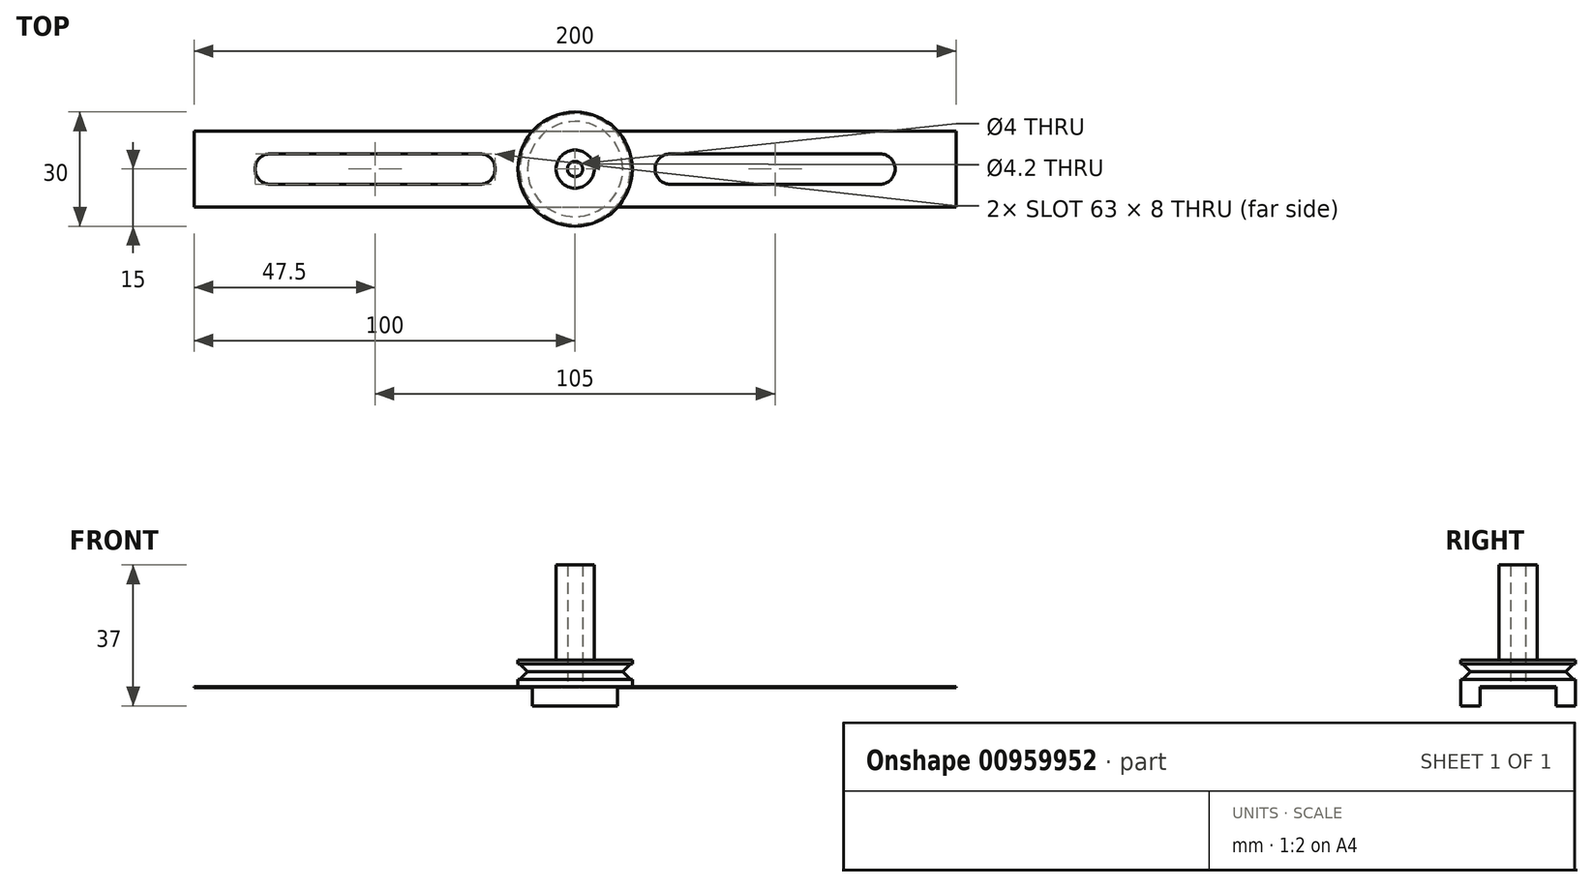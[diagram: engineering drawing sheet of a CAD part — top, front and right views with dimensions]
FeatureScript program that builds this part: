
annotation { "Feature Type Name" : "Feature", "Feature Type Description" : "" }
export const myFeature = defineFeature(function(context is Context, id is Id, definition is map)
    precondition{}
    {
        {
            var Q0;
            Q0=qCreatedBy(makeId("Top.planeOp"),FACE);
            var sketch = newSketch(context, id + "F0", { "sketchPlane" : qUnion([Q0])});
            skLineSegment(sketch, "E0.bottom", {"start": v(-100, 10) * mm, "end": v(100, 10) * mm});
            skLineSegment(sketch, "E0.top", {"start": v(-100, -10) * mm, "end": v(100, -10) * mm});
            skLineSegment(sketch, "E0.left", {"start": v(-100, 10) * mm, "end": v(-100, -10) * mm});
            skLineSegment(sketch, "E0.right", {"start": v(100, 10) * mm, "end": v(100, -10) * mm});
            skPoint(sketch, "E0.middle", {"position": v(0, 0) * mm});
            skSolve(sketch);
        }
        {
            var Q0;
            Q0 = qSketchRegion(id + "F0", true);
            extrude(context, id + "F1", {"entities" : qUnion([Q0]), "endBound" : BoundingType.SYMMETRIC, "oppositeDirection" : true, "depth" : 5 * mm, "offsetDistance" : 25 * mm});
        }
        {
            var Q0;
            Q0=qCreatedBy(makeId("Top.planeOp"),FACE);
            var sketch = newSketch(context, id + "F2", { "sketchPlane" : qUnion([Q0])});
            skCircle(sketch, "E1", {"center": v(0, 0) * mm, "radius": 2.1 * mm});
            skSolve(sketch);
        }
        {
            var Q0;
            Q0 = qSketchRegion(id + "F2", true);
            extrude(context, id + "F3", {"entities" : qUnion([Q0]), "operationType" : NewBodyOperationType.REMOVE, "endBound" : BoundingType.THROUGH_ALL, "depth" : 25 * mm, "offsetDistance" : 25 * mm, "hasSecondDirection" : true, "secondDirectionBound" : SecondDirectionBoundingType.THROUGH_ALL, "secondDirectionOppositeDirection" : true, "secondDirectionDepth" : 25 * mm});
        }
        {
            var Q0;
            Q0=qCreatedBy(makeId("Top.planeOp"),FACE);
            var sketch = newSketch(context, id + "F4", { "sketchPlane" : qUnion([Q0])});
            skLineSegment(sketch, "E2", {"start": v(0, 0) * mm, "end": v(0, 27.06) * mm, "construction": true});
            skLineSegment(sketch, "E3", {"start": v(-80, 0) * mm, "end": v(-25, 0) * mm});
            skArc(sketch, "E4.0.startCap", {"start": v(-80, -4) * mm, "mid": v(-84, 0) * mm, "end": v(-80, 4) * mm});
            skArc(sketch, "E4.0.endCap", {"start": v(-25, 4) * mm, "mid": v(-21, 0) * mm, "end": v(-25, -4) * mm});
            skLineSegment(sketch, "E4.0.left", {"start": v(-80, 4) * mm, "end": v(-25, 4) * mm});
            skLineSegment(sketch, "E4.0.right", {"start": v(-80, -4) * mm, "end": v(-25, -4) * mm});
            skArc(sketch, "E5.MirrorCS", {"start": v(25, 4) * mm, "mid": v(21, 0) * mm, "end": v(25, -4) * mm});
            skLineSegment(sketch, "E6.MirrorCS", {"start": v(80, 4) * mm, "end": v(25, 4) * mm});
            skLineSegment(sketch, "E7.MirrorCS", {"start": v(80, -4) * mm, "end": v(25, -4) * mm});
            skArc(sketch, "E8.MirrorCS", {"start": v(80, -4) * mm, "mid": v(84, 0) * mm, "end": v(80, 4) * mm});
            skSolve(sketch);
        }
        {
            var Q0;
            Q0 = qSketchRegion(id + "F4", true);
            extrude(context, id + "F5", {"entities" : qUnion([Q0]), "operationType" : NewBodyOperationType.REMOVE, "endBound" : BoundingType.SYMMETRIC, "depth" : 25 * mm, "offsetDistance" : 25 * mm});
        }
        {
            var Q0;
            Q0=qCreatedBy(makeId("Front.planeOp"),FACE);
            var sketch = newSketch(context, id + "F6", { "sketchPlane" : qUnion([Q0])});
            skLineSegment(sketch, "E9", {"start": v(0, 0) * mm, "end": v(0, 37) * mm, "construction": true});
            skLineSegment(sketch, "E10", {"start": v(0, -2.5) * mm, "end": v(15, -2.5) * mm});
            skLineSegment(sketch, "E11", {"start": v(15, -2.5) * mm, "end": v(15, 9.5) * mm});
            skLineSegment(sketch, "E12", {"start": v(15, 9.5) * mm, "end": v(5, 9.5) * mm});
            skLineSegment(sketch, "E13", {"start": v(5, 9.5) * mm, "end": v(5, 34.5) * mm});
            skLineSegment(sketch, "E14", {"start": v(5, 34.5) * mm, "end": v(0, 34.5) * mm});
            skLineSegment(sketch, "E15", {"start": v(0, 34.5) * mm, "end": v(0, -2.5) * mm});
            skSolve(sketch);
        }
        {
            var Q0;
            Q0 = qSketchRegion(id + "F6", true);
            var Q1;
            Q1=sQuery(id+"F6.wireOp",EDGE,"E9");
            revolve(context, id + "F7", {"surfaceOperationType" : NewSurfaceOperationType.NEW, "entities" : qUnion([Q0]), "axis" : qUnion([Q1]), "revolveType" : RevolveType.FULL});
        }
        {
            var Q0;
            Q0=qCreatedBy(makeId("Front.planeOp"),FACE);
            var sketch = newSketch(context, id + "F8", { "sketchPlane" : qUnion([Q0])});
            skLineSegment(sketch, "E16", {"start": v(15, 8.5) * mm, "end": v(14.5, 8.5) * mm});
            skLineSegment(sketch, "E17", {"start": v(14.5, 8.5) * mm, "end": v(12.5, 6.5) * mm});
            skLineSegment(sketch, "E18", {"start": v(12.5, 6.5) * mm, "end": v(14.5, 4.5) * mm});
            skLineSegment(sketch, "E19", {"start": v(14.5, 4.5) * mm, "end": v(15, 4.5) * mm});
            skLineSegment(sketch, "E20", {"start": v(15, 4.5) * mm, "end": v(15, 8.5) * mm});
            skLineSegment(sketch, "E21", {"start": v(15, 6.5) * mm, "end": v(12.5, 6.5) * mm, "construction": true});
            skSolve(sketch);
        }
        {
            var Q0;
            Q0 = qSketchRegion(id + "F8", true);
            var Q1;
            Q1=sQuery(id+"F6.wireOp",EDGE,"E15");
            revolve(context, id + "F9", {"operationType" : NewBodyOperationType.REMOVE, "surfaceOperationType" : NewSurfaceOperationType.NEW, "entities" : qUnion([Q0]), "axis" : qUnion([Q1]), "revolveType" : RevolveType.FULL, "oppositeDirection" : true});
        }
        {
            var Q0;
            Q0=makeQuery(id+"F7.opRevolve","SWEPT_FACE",FACE,{"disambiguationData":[OSD([sQuery(id+"F6.wireOp",EDGE,"E10")])]});
            var sketch = newSketch(context, id + "F10", { "sketchPlane" : qUnion([Q0])});
            skLineSegment(sketch, "E22.0", {"start": v(-100, 10) * mm, "end": v(100, 10) * mm});
            skLineSegment(sketch, "E22.1", {"start": v(-100, -10) * mm, "end": v(-100, 10) * mm});
            skLineSegment(sketch, "E22.2", {"start": v(-100, -10) * mm, "end": v(100, -10) * mm});
            skLineSegment(sketch, "E22.3", {"start": v(100, -10) * mm, "end": v(100, 10) * mm});
            skSolve(sketch);
        }
        {
            var Q0;
            Q0 = qSketchRegion(id + "F10", true);
            extrude(context, id + "F11", {"entities" : qUnion([Q0]), "operationType" : NewBodyOperationType.REMOVE, "oppositeDirection" : true, "depth" : 4.75 * mm, "offsetDistance" : 25 * mm});
        }
        {
            var Q0;
            Q0=makeQuery(id+"F11.boolean.opBoolean","COPY",FACE,{"derivedFrom":makeQuery(id+"F11.opExtrude","CAP_FACE",FACE,{"disambiguationData":[OSD([sQuery(id+"F10.wireOp",EDGE,"E22.0"),sQuery(id+"F10.wireOp",EDGE,"E22.1"),sQuery(id+"F10.wireOp",EDGE,"E22.2"),sQuery(id+"F10.wireOp",EDGE,"E22.3")])],"isStart":false})});
            var sketch = newSketch(context, id + "F12", { "sketchPlane" : qUnion([Q0])});
            skCircle(sketch, "E23", {"center": v(0, 0) * mm, "radius": 2 * mm});
            skSolve(sketch);
        }
        {
            var Q0;
            Q0 = qSketchRegion(id + "F12", true);
            extrude(context, id + "F13", {"entities" : qUnion([Q0]), "operationType" : NewBodyOperationType.REMOVE, "endBound" : BoundingType.THROUGH_ALL, "oppositeDirection" : true, "depth" : 25 * mm, "offsetDistance" : 25 * mm});
        }
    });
